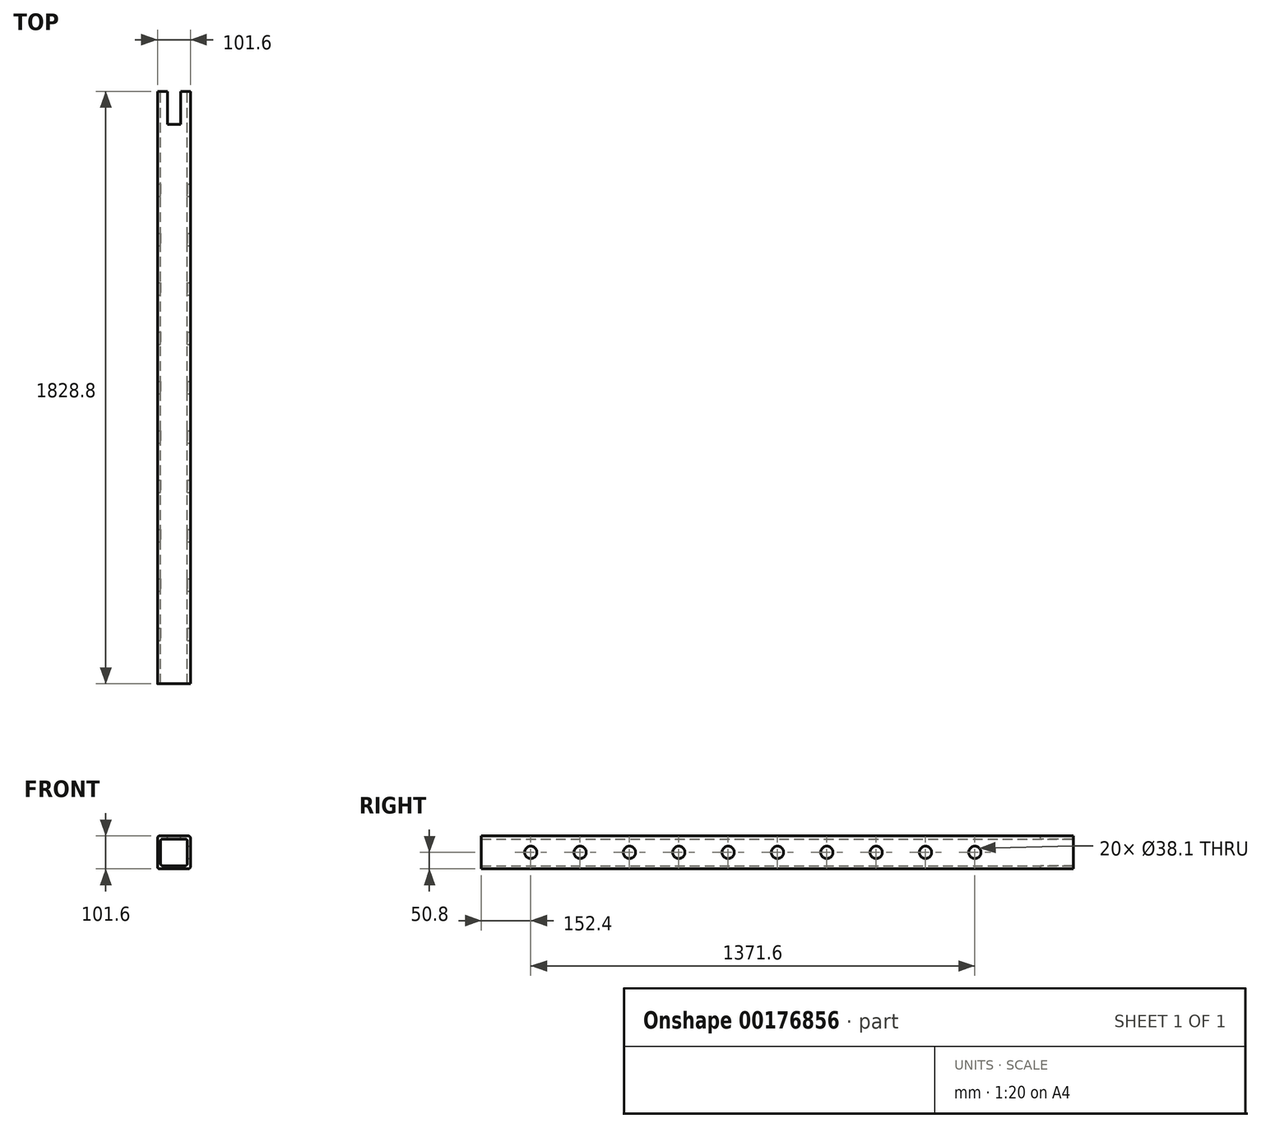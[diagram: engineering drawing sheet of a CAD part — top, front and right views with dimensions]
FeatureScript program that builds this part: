
annotation { "Feature Type Name" : "Feature", "Feature Type Description" : "" }
export const myFeature = defineFeature(function(context is Context, id is Id, definition is map)
    precondition{}
    {
        {
            var Q0;
            Q0=qCreatedBy(makeId("Front.planeOp"),FACE);
            var sketch = newSketch(context, id + "F0", { "sketchPlane" : qUnion([Q0])});
            skLineSegment(sketch, "E0.bottom", {"start": v(44.45, 50.8) * mm, "end": v(-44.45, 50.8) * mm});
            skLineSegment(sketch, "E0.top", {"start": v(44.45, -50.8) * mm, "end": v(-44.45, -50.8) * mm});
            skLineSegment(sketch, "E0.left", {"start": v(50.8, 44.45) * mm, "end": v(50.8, -44.45) * mm});
            skLineSegment(sketch, "E0.right", {"start": v(-50.8, 44.45) * mm, "end": v(-50.8, -44.45) * mm});
            skPoint(sketch, "E0.middle", {"position": v(0, 0) * mm});
            skLineSegment(sketch, "E1.bottom", {"start": v(34.93, 41.28) * mm, "end": v(-34.93, 41.28) * mm});
            skLineSegment(sketch, "E1.top", {"start": v(34.93, -41.28) * mm, "end": v(-34.93, -41.28) * mm});
            skLineSegment(sketch, "E1.left", {"start": v(41.28, 34.93) * mm, "end": v(41.28, -34.93) * mm});
            skLineSegment(sketch, "E1.right", {"start": v(-41.28, 34.93) * mm, "end": v(-41.28, -34.93) * mm});
            skPoint(sketch, "E2.visualSharp", {"position": v(-41.28, 41.28) * mm});
            skArc(sketch, "E2.filletArc", {"start": v(-34.93, 41.28) * mm, "mid": v(-39.42, 39.42) * mm, "end": v(-41.28, 34.93) * mm});
            skPoint(sketch, "E3.visualSharp", {"position": v(41.28, 41.28) * mm});
            skArc(sketch, "E3.filletArc", {"start": v(41.28, 34.93) * mm, "mid": v(39.42, 39.42) * mm, "end": v(34.93, 41.28) * mm});
            skPoint(sketch, "E4.visualSharp", {"position": v(50.8, 50.8) * mm});
            skArc(sketch, "E4.filletArc", {"start": v(50.8, 44.45) * mm, "mid": v(48.94, 48.94) * mm, "end": v(44.45, 50.8) * mm});
            skPoint(sketch, "E5.visualSharp", {"position": v(-50.8, 50.8) * mm});
            skArc(sketch, "E5.filletArc", {"start": v(-44.45, 50.8) * mm, "mid": v(-48.94, 48.94) * mm, "end": v(-50.8, 44.45) * mm});
            skPoint(sketch, "E6.visualSharp", {"position": v(-41.28, -41.28) * mm});
            skArc(sketch, "E6.filletArc", {"start": v(-41.28, -34.93) * mm, "mid": v(-39.42, -39.42) * mm, "end": v(-34.93, -41.28) * mm});
            skPoint(sketch, "E7.visualSharp", {"position": v(-50.8, -50.8) * mm});
            skArc(sketch, "E7.filletArc", {"start": v(-50.8, -44.45) * mm, "mid": v(-48.94, -48.94) * mm, "end": v(-44.45, -50.8) * mm});
            skPoint(sketch, "E8.visualSharp", {"position": v(41.28, -41.28) * mm});
            skArc(sketch, "E8.filletArc", {"start": v(34.93, -41.28) * mm, "mid": v(39.42, -39.42) * mm, "end": v(41.28, -34.93) * mm});
            skPoint(sketch, "E9.visualSharp", {"position": v(50.8, -50.8) * mm});
            skArc(sketch, "E9.filletArc", {"start": v(44.45, -50.8) * mm, "mid": v(48.94, -48.94) * mm, "end": v(50.8, -44.45) * mm});
            skSolve(sketch);
        }
        {
            var Q0;
            Q0 = qSketchRegion(id + "F0", true);
            extrude(context, id + "F1", {"entities" : qUnion([Q0]), "endBound" : BoundingType.SYMMETRIC, "depth" : 1828.8 * mm});
        }
        {
            var Q0;
            Q0=makeQuery(id+"F1.opExtrude","SWEPT_FACE",FACE,{"disambiguationData":[OSD([sQuery(id+"F0.wireOp",EDGE,"E0.left")])]});
            var sketch = newSketch(context, id + "F2", { "sketchPlane" : qUnion([Q0])});
            skCircle(sketch, "E10", {"center": v(-762, 0) * mm, "radius": 19.05 * mm});
            skPoint(sketch, "E10.centerSnap0", {"position": v(-914.4, 0) * mm});
            skCircle(sketch, "E11.1.0.0", {"center": v(-609.6, 0) * mm, "radius": 19.05 * mm});
            skCircle(sketch, "E11.2.0.0", {"center": v(-457.2, 0) * mm, "radius": 19.05 * mm});
            skCircle(sketch, "E11.3.0.0", {"center": v(-304.8, 0) * mm, "radius": 19.05 * mm});
            skCircle(sketch, "E11.4.0.0", {"center": v(-152.4, 0) * mm, "radius": 19.05 * mm});
            skCircle(sketch, "E11.5.0.0", {"center": v(0, 0) * mm, "radius": 19.05 * mm});
            skCircle(sketch, "E11.6.0.0", {"center": v(152.4, 0) * mm, "radius": 19.05 * mm});
            skCircle(sketch, "E11.7.0.0", {"center": v(304.8, 0) * mm, "radius": 19.05 * mm});
            skCircle(sketch, "E11.8.0.0", {"center": v(457.2, 0) * mm, "radius": 19.05 * mm});
            skCircle(sketch, "E11.9.0.0", {"center": v(609.6, 0) * mm, "radius": 19.05 * mm});
            skLineSegment(sketch, "E11.direction1", {"start": v(-762, 0) * mm, "end": v(-609.6, 0) * mm, "construction": true});
            skSolve(sketch);
        }
        {
            var Q0;
            Q0=makeQuery(id+"F2.imprint","IMPRINT",FACE,{"disambiguationData":[TD([[makeQuery(id+"F2.imprint","IMPRINT",EDGE,{"derivedFrom":sQuery(id+"F2.wireOp",EDGE,"E11.7.0.0")}),1.0]])]});
            var Q1;
            Q1=makeQuery(id+"F2.imprint","IMPRINT",FACE,{"disambiguationData":[TD([[makeQuery(id+"F2.imprint","IMPRINT",EDGE,{"derivedFrom":sQuery(id+"F2.wireOp",EDGE,"E10")}),1.0]])]});
            var Q2;
            Q2=makeQuery(id+"F2.imprint","IMPRINT",FACE,{"disambiguationData":[TD([[makeQuery(id+"F2.imprint","IMPRINT",EDGE,{"derivedFrom":sQuery(id+"F2.wireOp",EDGE,"E11.1.0.0")}),1.0]])]});
            var Q3;
            Q3=makeQuery(id+"F2.imprint","IMPRINT",FACE,{"disambiguationData":[TD([[makeQuery(id+"F2.imprint","IMPRINT",EDGE,{"derivedFrom":sQuery(id+"F2.wireOp",EDGE,"E11.2.0.0")}),1.0]])]});
            var Q4;
            Q4=makeQuery(id+"F2.imprint","IMPRINT",FACE,{"disambiguationData":[TD([[makeQuery(id+"F2.imprint","IMPRINT",EDGE,{"derivedFrom":sQuery(id+"F2.wireOp",EDGE,"E11.3.0.0")}),1.0]])]});
            var Q5;
            Q5=makeQuery(id+"F2.imprint","IMPRINT",FACE,{"disambiguationData":[TD([[makeQuery(id+"F2.imprint","IMPRINT",EDGE,{"derivedFrom":sQuery(id+"F2.wireOp",EDGE,"E11.4.0.0")}),1.0]])]});
            var Q6;
            Q6=makeQuery(id+"F2.imprint","IMPRINT",FACE,{"disambiguationData":[TD([[makeQuery(id+"F2.imprint","IMPRINT",EDGE,{"derivedFrom":sQuery(id+"F2.wireOp",EDGE,"E11.5.0.0")}),1.0]])]});
            var Q7;
            Q7=makeQuery(id+"F2.imprint","IMPRINT",FACE,{"disambiguationData":[TD([[makeQuery(id+"F2.imprint","IMPRINT",EDGE,{"derivedFrom":sQuery(id+"F2.wireOp",EDGE,"E11.6.0.0")}),1.0]])]});
            var Q8;
            Q8=makeQuery(id+"F2.imprint","IMPRINT",FACE,{"disambiguationData":[TD([[makeQuery(id+"F2.imprint","IMPRINT",EDGE,{"derivedFrom":sQuery(id+"F2.wireOp",EDGE,"E11.8.0.0")}),1.0]])]});
            var Q9;
            Q9=makeQuery(id+"F2.imprint","IMPRINT",FACE,{"disambiguationData":[TD([[makeQuery(id+"F2.imprint","IMPRINT",EDGE,{"derivedFrom":sQuery(id+"F2.wireOp",EDGE,"E11.9.0.0")}),1.0]])]});
            extrude(context, id + "F3", {"entities" : qUnion([Q0, Q1, Q2, Q3, Q4, Q5, Q6, Q7, Q8, Q9]), "operationType" : NewBodyOperationType.REMOVE, "oppositeDirection" : true, "depth" : 127 * mm});
        }
        {
            var Q0;
            Q0=makeQuery(id+"F1.opExtrude","SWEPT_FACE",FACE,{"disambiguationData":[OSD([sQuery(id+"F0.wireOp",EDGE,"E0.bottom")])]});
            var sketch = newSketch(context, id + "F4", { "sketchPlane" : qUnion([Q0])});
            skLineSegment(sketch, "E12.bottom", {"start": v(-20.57, 812.8) * mm, "end": v(20.57, 812.8) * mm});
            skLineSegment(sketch, "E12.top", {"start": v(-20.57, 1016) * mm, "end": v(20.57, 1016) * mm});
            skLineSegment(sketch, "E12.left", {"start": v(-20.57, 812.8) * mm, "end": v(-20.57, 1016) * mm});
            skLineSegment(sketch, "E12.right", {"start": v(20.57, 812.8) * mm, "end": v(20.57, 1016) * mm});
            skPoint(sketch, "E12.middle", {"position": v(0, 914.4) * mm});
            skSolve(sketch);
        }
        {
            var Q0;
            Q0 = qSketchRegion(id + "F4", true);
            extrude(context, id + "F5", {"entities" : qUnion([Q0]), "operationType" : NewBodyOperationType.REMOVE, "oppositeDirection" : true, "depth" : 127 * mm});
        }
    });
